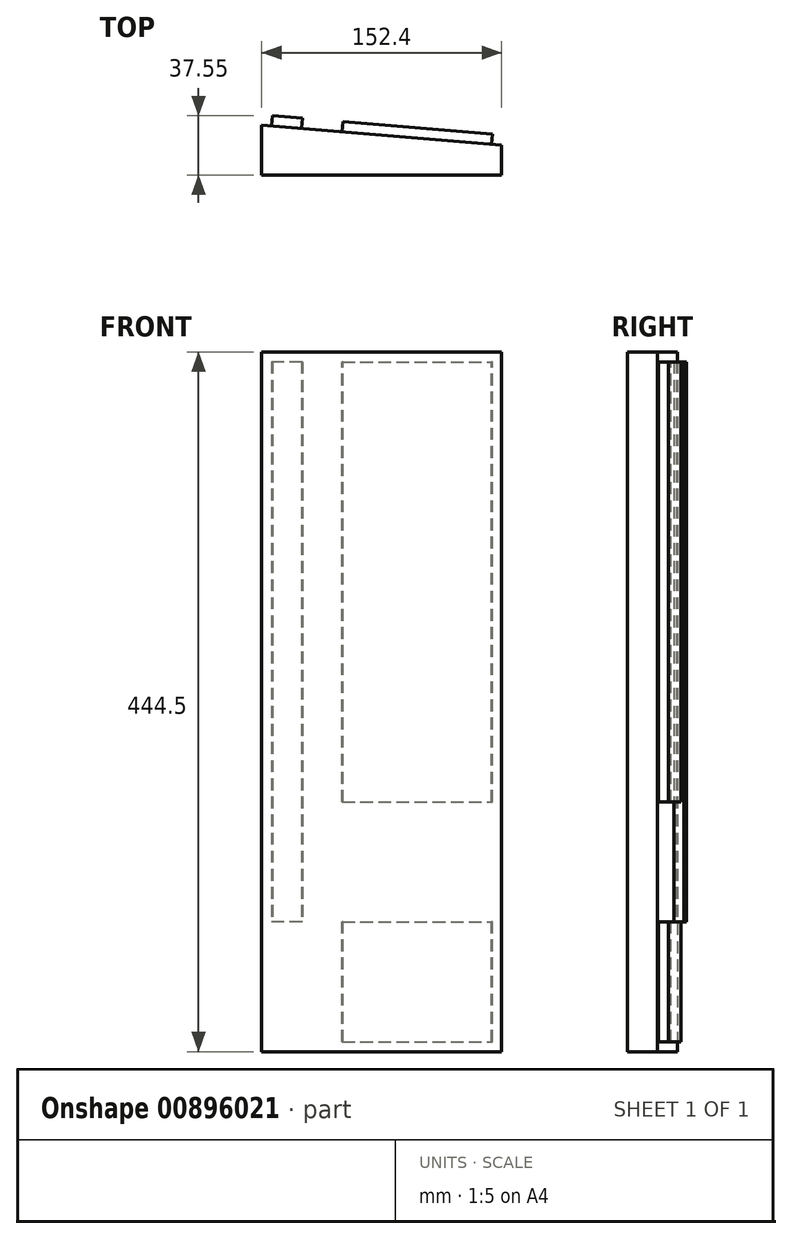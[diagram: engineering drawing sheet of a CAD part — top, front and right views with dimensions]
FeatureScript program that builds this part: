
annotation { "Feature Type Name" : "Feature", "Feature Type Description" : "" }
export const myFeature = defineFeature(function(context is Context, id is Id, definition is map)
    precondition{}
    {
        {
            var Q0;
            Q0=qCreatedBy(makeId("Top.planeOp"),FACE);
            var sketch = newSketch(context, id + "F0", { "sketchPlane" : qUnion([Q0])});
            skLineSegment(sketch, "E0", {"start": v(0, 0) * mm, "end": v(152.4, 0) * mm});
            skLineSegment(sketch, "E1", {"start": v(152.4, 0) * mm, "end": v(152.4, 19.05) * mm});
            skLineSegment(sketch, "E2", {"start": v(152.4, 19.05) * mm, "end": v(0, 31.75) * mm});
            skLineSegment(sketch, "E3", {"start": v(0, 31.75) * mm, "end": v(0, 0) * mm});
            skSolve(sketch);
        }
        {
            var Q0;
            Q0 = qSketchRegion(id + "F0", true);
            extrude(context, id + "F1", {"entities" : qUnion([Q0]), "depth" : 444.5 * mm, "offsetDistance" : 25.4 * mm});
        }
        {
            var Q0;
            Q0=makeQuery(id+"F1.opExtrude","SWEPT_FACE",FACE,{"disambiguationData":[OSD([sQuery(id+"F0.wireOp",EDGE,"E2")])]});
            var sketch = newSketch(context, id + "F2", { "sketchPlane" : qUnion([Q0])});
            skLineSegment(sketch, "E4.bottom", {"start": v(-48.7, 6.35) * mm, "end": v(-143.94, 6.35) * mm});
            skLineSegment(sketch, "E4.top", {"start": v(-48.7, 82.55) * mm, "end": v(-143.94, 82.55) * mm});
            skLineSegment(sketch, "E4.left", {"start": v(-48.7, 6.35) * mm, "end": v(-48.7, 82.55) * mm});
            skLineSegment(sketch, "E4.right", {"start": v(-143.94, 6.35) * mm, "end": v(-143.94, 82.55) * mm});
            skLineSegment(sketch, "E5.bottom", {"start": v(-48.7, 158.75) * mm, "end": v(-143.94, 158.75) * mm});
            skLineSegment(sketch, "E5.top", {"start": v(-48.7, 438.15) * mm, "end": v(-143.94, 438.15) * mm});
            skLineSegment(sketch, "E5.left", {"start": v(-48.7, 158.75) * mm, "end": v(-48.7, 438.15) * mm});
            skLineSegment(sketch, "E5.right", {"start": v(-143.94, 158.75) * mm, "end": v(-143.94, 438.15) * mm});
            skLineSegment(sketch, "E6.bottom", {"start": v(-22.76, 438.15) * mm, "end": v(-3.71, 438.15) * mm});
            skLineSegment(sketch, "E6.top", {"start": v(-22.76, 82.55) * mm, "end": v(-3.71, 82.55) * mm});
            skLineSegment(sketch, "E6.left", {"start": v(-22.76, 438.15) * mm, "end": v(-22.76, 82.55) * mm});
            skLineSegment(sketch, "E6.right", {"start": v(-3.71, 438.15) * mm, "end": v(-3.71, 82.55) * mm});
            skSolve(sketch);
        }
        {
            var Q0;
            Q0=makeQuery(id+"F2.imprint","IMPRINT",FACE,{"disambiguationData":[TD([[makeQuery(id+"F2.imprint","IMPRINT",EDGE,{"derivedFrom":sQuery(id+"F2.wireOp",EDGE,"E5.bottom")}),-1.0]])]});
            var Q1;
            Q1=makeQuery(id+"F2.imprint","IMPRINT",FACE,{"disambiguationData":[TD([[makeQuery(id+"F2.imprint","IMPRINT",EDGE,{"derivedFrom":sQuery(id+"F2.wireOp",EDGE,"E6.bottom")}),-1.0]])]});
            var Q2;
            Q2=makeQuery(id+"F2.imprint","IMPRINT",FACE,{"disambiguationData":[TD([[makeQuery(id+"F2.imprint","IMPRINT",EDGE,{"derivedFrom":sQuery(id+"F2.wireOp",EDGE,"E4.bottom")}),-1.0]])]});
            extrude(context, id + "F3", {"entities" : qUnion([Q0, Q1, Q2]), "operationType" : NewBodyOperationType.ADD, "depth" : 6.35 * mm, "offsetDistance" : 25.4 * mm});
        }
    });
